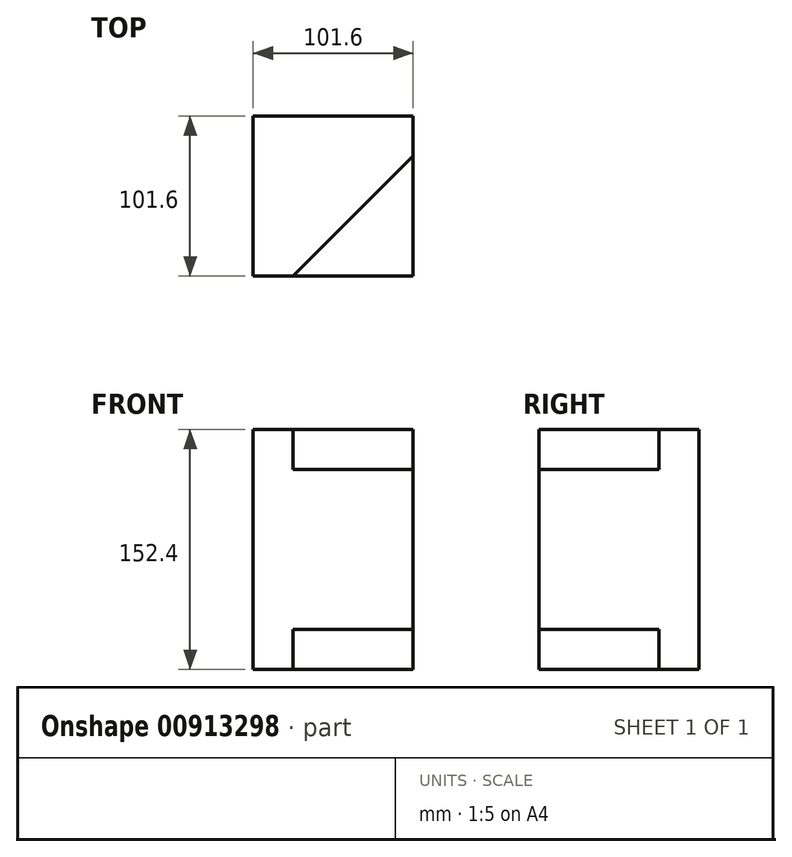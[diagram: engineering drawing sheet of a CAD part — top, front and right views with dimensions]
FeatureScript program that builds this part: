
annotation { "Feature Type Name" : "Feature", "Feature Type Description" : "" }
export const myFeature = defineFeature(function(context is Context, id is Id, definition is map)
    precondition{}
    {
        {
            var Q0;
            Q0=qCreatedBy(makeId("Top.planeOp"),FACE);
            var sketch = newSketch(context, id + "F0", { "sketchPlane" : qUnion([Q0])});
            skLineSegment(sketch, "E0.bottom", {"start": v(0, 0) * mm, "end": v(101.6, 0) * mm});
            skLineSegment(sketch, "E0.top", {"start": v(0, -101.6) * mm, "end": v(101.6, -101.6) * mm});
            skLineSegment(sketch, "E0.left", {"start": v(0, 0) * mm, "end": v(0, -101.6) * mm});
            skLineSegment(sketch, "E0.right", {"start": v(101.6, 0) * mm, "end": v(101.6, -101.6) * mm});
            skSolve(sketch);
        }
        {
            var Q0;
            Q0 = qSketchRegion(id + "F0", true);
            extrude(context, id + "F1", {"entities" : qUnion([Q0]), "depth" : 101.6 * mm, "offsetDistance" : 25.4 * mm});
        }
        {
            var Q0;
            Q0=makeQuery(id+"F1.opExtrude","CAP_FACE",FACE,{"disambiguationData":[OSD([sQuery(id+"F0.wireOp",EDGE,"E0.bottom"),sQuery(id+"F0.wireOp",EDGE,"E0.top"),sQuery(id+"F0.wireOp",EDGE,"E0.left"),sQuery(id+"F0.wireOp",EDGE,"E0.right")])],"isStart":false});
            var sketch = newSketch(context, id + "F2", { "sketchPlane" : qUnion([Q0])});
            skLineSegment(sketch, "E1.bottom", {"start": v(0, 0) * mm, "end": v(101.6, 0) * mm});
            skLineSegment(sketch, "E1.top", {"start": v(0, -101.6) * mm, "end": v(101.6, -101.6) * mm});
            skLineSegment(sketch, "E1.left", {"start": v(0, 0) * mm, "end": v(0, -101.6) * mm});
            skLineSegment(sketch, "E1.right", {"start": v(101.6, 0) * mm, "end": v(101.6, -101.6) * mm});
            skSolve(sketch);
        }
        {
            var Q0;
            Q0=makeQuery(id+"F2.imprint","IMPRINT",FACE,{"disambiguationData":[TD([[makeQuery(id+"F2.imprint","IMPRINT",EDGE,{"derivedFrom":sQuery(id+"F2.wireOp",EDGE,"E1.bottom")}),-1.0]])]});
            var sketch = newSketch(context, id + "F3", { "sketchPlane" : qUnion([Q0])});
            skLineSegment(sketch, "E2.bottom", {"start": v(0, 0) * mm, "end": v(101.6, 0) * mm});
            skLineSegment(sketch, "E2.top", {"start": v(0, -25.4) * mm, "end": v(101.6, -25.4) * mm});
            skLineSegment(sketch, "E2.left", {"start": v(0, 0) * mm, "end": v(0, -25.4) * mm});
            skLineSegment(sketch, "E2.right", {"start": v(101.6, 0) * mm, "end": v(101.6, -25.4) * mm});
            skSolve(sketch);
        }
        {
            var Q0;
            Q0 = qSketchRegion(id + "F3", true);
            extrude(context, id + "F4", {"entities" : qUnion([Q0]), "operationType" : NewBodyOperationType.ADD, "depth" : 25.4 * mm, "offsetDistance" : 25.4 * mm});
        }
        {
            var Q0;
            Q0=makeQuery(id+"F2.imprint","IMPRINT",FACE,{"disambiguationData":[TD([[makeQuery(id+"F2.imprint","IMPRINT",EDGE,{"derivedFrom":sQuery(id+"F2.wireOp",EDGE,"E1.bottom")}),-1.0]])]});
            var sketch = newSketch(context, id + "F5", { "sketchPlane" : qUnion([Q0])});
            skLineSegment(sketch, "E3.bottom", {"start": v(0, -101.3) * mm, "end": v(25.4, -101.3) * mm});
            skLineSegment(sketch, "E3.top", {"start": v(0, -25.1) * mm, "end": v(25.4, -25.1) * mm});
            skLineSegment(sketch, "E3.left", {"start": v(0, -101.3) * mm, "end": v(0, -25.1) * mm});
            skLineSegment(sketch, "E3.right", {"start": v(25.4, -101.3) * mm, "end": v(25.4, -25.1) * mm});
            skSolve(sketch);
        }
        {
            var Q0;
            Q0 = qSketchRegion(id + "F5", true);
            extrude(context, id + "F6", {"entities" : qUnion([Q0]), "operationType" : NewBodyOperationType.ADD, "depth" : 25.4 * mm, "offsetDistance" : 25.4 * mm});
        }
        {
            var Q0;
            Q0=makeQuery(id+"F2.imprint","IMPRINT",FACE,{"disambiguationData":[TD([[makeQuery(id+"F2.imprint","IMPRINT",EDGE,{"derivedFrom":sQuery(id+"F2.wireOp",EDGE,"E1.bottom")}),-1.0]])]});
            var sketch = newSketch(context, id + "F7", { "sketchPlane" : qUnion([Q0])});
            skLineSegment(sketch, "E4.bottom", {"start": v(0, 0) * mm, "end": v(101.6, 0) * mm});
            skLineSegment(sketch, "E4.top", {"start": v(0, -101.6) * mm, "end": v(25.4, -101.6) * mm});
            skLineSegment(sketch, "E4.left", {"start": v(0, 0) * mm, "end": v(0, -101.6) * mm});
            skLineSegment(sketch, "E4.right", {"start": v(101.6, 0) * mm, "end": v(101.6, -25.4) * mm});
            skLineSegment(sketch, "E5", {"start": v(101.6, -25.4) * mm, "end": v(25.4, -101.6) * mm});
            skLineSegment(sketch, "E6", {"start": v(25.4, -101.6) * mm, "end": v(25.4, -25.4) * mm});
            skLineSegment(sketch, "E7", {"start": v(25.4, -25.4) * mm, "end": v(101.6, -25.4) * mm});
            skSolve(sketch);
        }
        {
            var Q0;
            Q0 = qSketchRegion(id + "F7", true);
            extrude(context, id + "F8", {"entities" : qUnion([Q0]), "operationType" : NewBodyOperationType.ADD, "depth" : 25.4 * mm, "offsetDistance" : 25.4 * mm});
        }
        {
            var Q0;
            Q0=makeQuery(id+"F1.opExtrude","CAP_FACE",FACE,{"disambiguationData":[OSD([sQuery(id+"F0.wireOp",EDGE,"E0.bottom"),sQuery(id+"F0.wireOp",EDGE,"E0.top"),sQuery(id+"F0.wireOp",EDGE,"E0.left"),sQuery(id+"F0.wireOp",EDGE,"E0.right")])],"isStart":true});
            var sketch = newSketch(context, id + "F9", { "sketchPlane" : qUnion([Q0])});
            skLineSegment(sketch, "E8.bottom", {"start": v(0, 0) * mm, "end": v(101.6, 0) * mm});
            skLineSegment(sketch, "E8.top", {"start": v(0, 101.6) * mm, "end": v(25.4, 101.6) * mm});
            skLineSegment(sketch, "E8.left", {"start": v(0, 0) * mm, "end": v(0, 101.6) * mm});
            skLineSegment(sketch, "E8.right", {"start": v(101.6, 0) * mm, "end": v(101.6, 25.4) * mm});
            skLineSegment(sketch, "E9", {"start": v(25.4, 101.6) * mm, "end": v(101.6, 25.4) * mm});
            skSolve(sketch);
        }
        {
            var Q0;
            Q0 = qSketchRegion(id + "F9", true);
            extrude(context, id + "F10", {"entities" : qUnion([Q0]), "operationType" : NewBodyOperationType.ADD, "depth" : 25.4 * mm, "offsetDistance" : 25.4 * mm});
        }
    });
